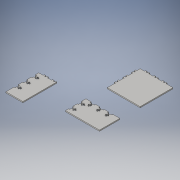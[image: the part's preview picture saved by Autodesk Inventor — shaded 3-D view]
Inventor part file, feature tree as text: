
AUTODESK INVENTOR PART (.ipt)
format: ipt  version: 2016 (Build 200138000, 138)  size: 391,680 bytes
history: native  units: in
note: dims shown in document units (in); Inventor stores cm internally (conversion verified against a paired STEP export)
features: extrude x9, sketch x9, pattern_linear x6
ambient origin geometry x8: Origin, YZ Plane, XZ Plane, XY Plane, X Axis, Y Axis, Z Axis, Center Point
bodies: Solid1 (feature_tree)
feature tree (24):
  extrude  "Extrusion1"  Depth=3.937in
  extrude  "Extrusion2"  Depth=3.937in
  pattern_linear  "Rectangular Pattern1"  Count1=10  [1 undecoded]
  extrude  "Extrusion3"  Depth=0.125in TaperAngle=0.0deg
  pattern_linear  "Rectangular Pattern2"  Count1=3  [1 undecoded]
  extrude  "Extrusion4"  Depth=0.5in
  extrude  "Extrusion5"  Depth=0.181in
  extrude  "Extrusion6"  Depth=0.125in TaperAngle=0.0deg
  pattern_linear  "Rectangular Pattern3"  Count1=3 Spacing1=1.0in
  extrude  "Extrusion7"  Depth=0.125in
  pattern_linear  "Rectangular Pattern4"  Spacing1=0.125in  [1 undecoded]
  extrude  "Extrusion8"  Depth=1.1811in
  pattern_linear  "Rectangular Pattern5"  Spacing1=0.125in  [1 undecoded]
  extrude  "Extrusion9"  Depth=0.181in
  pattern_linear  "Rectangular Pattern6"  Spacing1=0.125in  [1 undecoded]
  sketch  "Sketch1"  dims[d0=1.9685in d1=3.937in]
  sketch  "Sketch2"  dims[d2=2.3622in d3=3.937in d4=3.937in]
  sketch  "Sketch3"  dims[d5=3.937in d6=0.125in d7=0.0in d8=1.1811in]
  sketch  "Sketch4"  dims[d9=1.1811in d10=0.5in]
  sketch  "Sketch5"  dims[d11=0.125in d12=0.181in]
  sketch  "Sketch6"  dims[d13=0.138in d14=0.125in d15=0.0in d16=1.1811in d18=1.0in]
  sketch  "Sketch7"  dims[d19=0.5in d20=0.125in]
  sketch  "Sketch8"  dims[d21=0.181in]
  sketch  "Sketch9"  dims[d22=0.138in d23=0.125in d24=0.0in d25=1.1811in d27=1.0in d29=0.125in d30=0.181in d31=0.125in d32=0.0in d34=0.125in d35=0.181in d36=0.125in d37=0.0in d38=0.5in d39=0.5in d40=0.125in d41=0.2362in d42=0.18in d43=0.14in d44=0.3125in d45=0.0937in d46=0.1094in d47=0.1294in d48=0.14in d49=0.0863in d50=0.125in d51=0.0in d52=1.1811in d54=1.0in d55=0.0in d56=0.625in d57=0.5in d58=0.125in d59=0.2362in d60=0.14in d61=0.18in d62=0.3125in d63=0.1094in d64=0.0937in d65=0.1294in d66=0.14in d67=0.0863in d68=0.125in d69=0.0in d70=1.1811in d72=1.0in d73=0.0in d74=0.125in d75=0.5in d76=0.181in d77=0.125in d78=0.138in d79=0.125in d80=0.0in d81=0.7874in d83=1.0in d84=0.5in d85=0.5in d86=0.125in d87=0.2362in d88=0.18in d89=0.14in d90=0.3125in d91=0.0937in d92=0.1094in d93=0.14in d94=0.1294in d95=0.0863in d96=0.125in d97=0.0in d98=0.7874in d100=1.0in]
note: 5 required parameter values undecoded (feature->parameter linkage not recoverable at this tier; creation-order binding heuristic only, values carry confidence <= 0.55)
